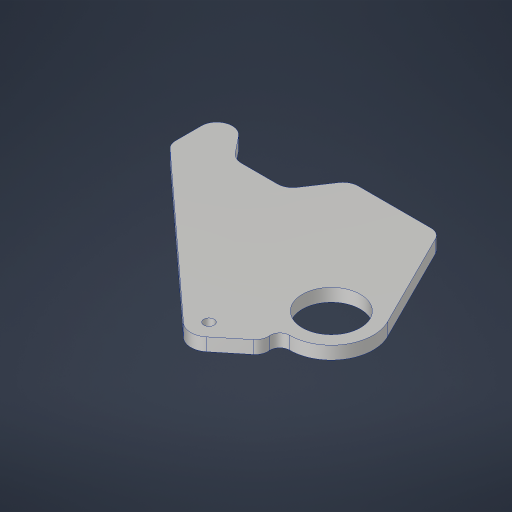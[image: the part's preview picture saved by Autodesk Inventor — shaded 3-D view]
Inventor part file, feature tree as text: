
AUTODESK INVENTOR PART (.ipt)
format: ipt  version: 2023.4 (Build 274418000, 418)  size: 238,592 bytes
history: native  units: in
note: dims shown in document units (in); Inventor stores cm internally (conversion verified against a paired STEP export)
features: fillet x2, sketch x1, extrude x1, hole x1
ambient origin geometry x8: Origin, YZ Plane, XZ Plane, XY Plane, X Axis, Y Axis, Z Axis, Center Point
bodies: Solid1 (feature_tree)
feature tree (5):
  sketch  "Sketch1"  dims[d0=1.315in d1=1.125in d2=0.25in d3=0.375in d4=1.0in d5=0.201in d6=0.25in d7=1.0in d8=0.375in d9=1.0in d10=2.0in d11=0.75in d12=0.5in d13=1.0in d15=3.0in d16=3.0in d17=0.5in d18=0.125in d19=0.375in d20=1.0in d21=0.125in d22=2.4849in d23=0.25in d24=0.0in d25=0.25in d26=0.3in d27=0.201in d28=0.75in d29=0.385in d30=0.25in d31=0.5635in d32=1.0in d33=0.8108in]
  extrude  "Extrusion1"  Depth=1.0in
  fillet  "Fillet1"  Radius=0.25in
  fillet  "Fillet2"  Radius=0.375in
  hole  "Hole1"  [1 undecoded]
note: 1 required parameter value undecoded (feature->parameter linkage not recoverable at this tier; creation-order binding heuristic only, values carry confidence <= 0.55)
